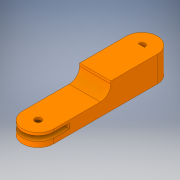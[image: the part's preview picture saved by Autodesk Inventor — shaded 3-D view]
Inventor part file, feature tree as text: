
AUTODESK INVENTOR PART (.ipt)
format: ipt  version: 2017 (Build 210142000, 142)  size: 159,232 bytes
history: native  units: in
note: dims shown in document units (in); Inventor stores cm internally (conversion verified against a paired STEP export)
features: extrude x3, sketch x2, fillet x1
ambient origin geometry x8: Origin, YZ Plane, XZ Plane, XY Plane, X Axis, Y Axis, Z Axis, Center Point
bodies: Solid1 (feature_tree)
feature tree (6):
  extrude  "Extrusion1"  Depth=0.75in
  extrude  "Extrusion3"  TaperAngle=0.0deg  [1 undecoded]
  fillet  "Fillet3"  Radius=0.25in
  extrude  "Extrusion4"  Depth=0.3937in TaperAngle=0.0deg
  sketch  "Sketch1"  dims[d0=1.5in d2=0.75in]
  sketch  "Sketch4"  dims[d3=0.3125in d6=0.0in d15=0.25in d17=0.3937in d18=0.0in d19=0.25in d20=0.625in d21=3.5in d22=0.5in d23=0.25in d24=1.0in d25=0.0in]
note: 1 required parameter value undecoded (feature->parameter linkage not recoverable at this tier; creation-order binding heuristic only, values carry confidence <= 0.55)
